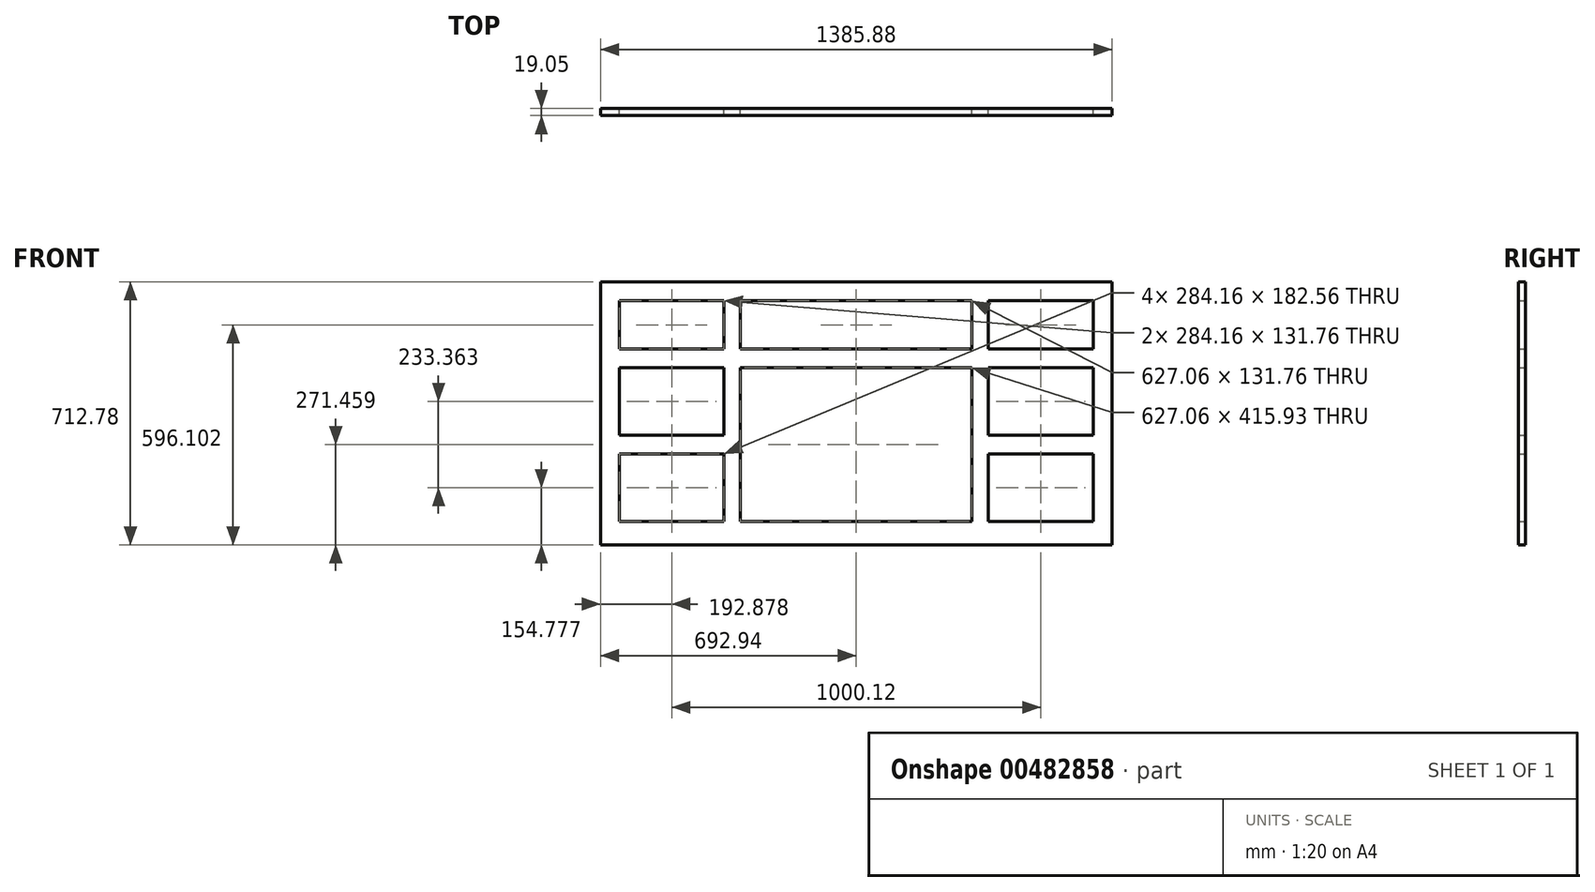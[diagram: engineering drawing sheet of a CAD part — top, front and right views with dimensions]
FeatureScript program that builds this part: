
annotation { "Feature Type Name" : "Feature", "Feature Type Description" : "" }
export const myFeature = defineFeature(function(context is Context, id is Id, definition is map)
    precondition{}
    {
        {
            var Q0;
            Q0=qCreatedBy(makeId("Front.planeOp"),FACE);
            var sketch = newSketch(context, id + "F0", { "sketchPlane" : qUnion([Q0])});
            skLineSegment(sketch, "E0.bottom", {"start": v(692.94, 356.4) * mm, "end": v(-692.94, 356.4) * mm});
            skLineSegment(sketch, "E0.top", {"start": v(692.94, -356.4) * mm, "end": v(-692.94, -356.4) * mm});
            skLineSegment(sketch, "E0.left", {"start": v(692.94, 356.4) * mm, "end": v(692.94, -356.4) * mm});
            skLineSegment(sketch, "E0.right", {"start": v(-692.94, 356.4) * mm, "end": v(-692.94, -356.4) * mm});
            skPoint(sketch, "E0.middle", {"position": v(0, 0) * mm});
            skLineSegment(sketch, "E1.bottom", {"start": v(-642.14, 305.6) * mm, "end": v(-357.98, 305.6) * mm});
            skLineSegment(sketch, "E1.top", {"start": v(-642.14, 173.83) * mm, "end": v(-357.98, 173.83) * mm});
            skLineSegment(sketch, "E1.left", {"start": v(-642.14, 305.6) * mm, "end": v(-642.14, 173.83) * mm});
            skLineSegment(sketch, "E1.right", {"start": v(-357.98, 305.6) * mm, "end": v(-357.98, 173.83) * mm});
            skLineSegment(sketch, "E2.bottom", {"start": v(-642.14, 123.03) * mm, "end": v(-357.98, 123.03) * mm});
            skLineSegment(sketch, "E2.top", {"start": v(-642.14, -59.53) * mm, "end": v(-357.98, -59.53) * mm});
            skLineSegment(sketch, "E2.left", {"start": v(-642.14, 123.03) * mm, "end": v(-642.14, -59.53) * mm});
            skLineSegment(sketch, "E2.right", {"start": v(-357.98, 123.03) * mm, "end": v(-357.98, -59.53) * mm});
            skLineSegment(sketch, "E3.bottom", {"start": v(-642.14, -110.33) * mm, "end": v(-357.98, -110.33) * mm});
            skLineSegment(sketch, "E3.top", {"start": v(-642.14, -292.9) * mm, "end": v(-357.98, -292.9) * mm});
            skLineSegment(sketch, "E3.left", {"start": v(-642.14, -110.33) * mm, "end": v(-642.14, -292.9) * mm});
            skLineSegment(sketch, "E3.right", {"start": v(-357.98, -110.33) * mm, "end": v(-357.98, -292.9) * mm});
            skLineSegment(sketch, "E4.bottom", {"start": v(-313.53, 305.6) * mm, "end": v(313.53, 305.6) * mm});
            skLineSegment(sketch, "E4.top", {"start": v(-313.53, 173.83) * mm, "end": v(313.53, 173.83) * mm});
            skLineSegment(sketch, "E4.left", {"start": v(-313.53, 305.6) * mm, "end": v(-313.53, 173.83) * mm});
            skLineSegment(sketch, "E4.right", {"start": v(313.53, 305.6) * mm, "end": v(313.53, 173.83) * mm});
            skLineSegment(sketch, "E5.bottom", {"start": v(357.98, 305.6) * mm, "end": v(642.14, 305.6) * mm});
            skLineSegment(sketch, "E5.top", {"start": v(357.98, 173.83) * mm, "end": v(642.14, 173.83) * mm});
            skLineSegment(sketch, "E5.left", {"start": v(357.98, 305.6) * mm, "end": v(357.98, 173.83) * mm});
            skLineSegment(sketch, "E5.right", {"start": v(642.14, 305.6) * mm, "end": v(642.14, 173.83) * mm});
            skLineSegment(sketch, "E6.bottom", {"start": v(357.98, 123.03) * mm, "end": v(642.14, 123.03) * mm});
            skLineSegment(sketch, "E6.top", {"start": v(357.98, -59.53) * mm, "end": v(642.14, -59.53) * mm});
            skLineSegment(sketch, "E6.left", {"start": v(357.98, 123.03) * mm, "end": v(357.98, -59.53) * mm});
            skLineSegment(sketch, "E6.right", {"start": v(642.14, 123.03) * mm, "end": v(642.14, -59.53) * mm});
            skLineSegment(sketch, "E7.bottom", {"start": v(357.98, -110.33) * mm, "end": v(642.14, -110.33) * mm});
            skLineSegment(sketch, "E7.top", {"start": v(357.98, -292.9) * mm, "end": v(642.14, -292.9) * mm});
            skLineSegment(sketch, "E7.left", {"start": v(357.98, -110.33) * mm, "end": v(357.98, -292.9) * mm});
            skLineSegment(sketch, "E7.right", {"start": v(642.14, -110.33) * mm, "end": v(642.14, -292.9) * mm});
            skLineSegment(sketch, "E8.bottom", {"start": v(-313.53, 123.03) * mm, "end": v(313.53, 123.03) * mm});
            skLineSegment(sketch, "E8.top", {"start": v(-313.53, -292.9) * mm, "end": v(313.53, -292.9) * mm});
            skLineSegment(sketch, "E8.left", {"start": v(-313.53, 123.03) * mm, "end": v(-313.53, -292.9) * mm});
            skLineSegment(sketch, "E8.right", {"start": v(313.53, 123.03) * mm, "end": v(313.53, -292.9) * mm});
            skSolve(sketch);
        }
        {
            var Q0;
            Q0=makeQuery(id+"F0.imprint","IMPRINT",FACE,{"disambiguationData":[TD([[makeQuery(id+"F0.imprint","IMPRINT",EDGE,{"derivedFrom":sQuery(id+"F0.wireOp",EDGE,"E0.bottom")}),1.0]])]});
            extrude(context, id + "F1", {"entities" : qUnion([Q0]), "depth" : 19.05 * mm});
        }
    });
